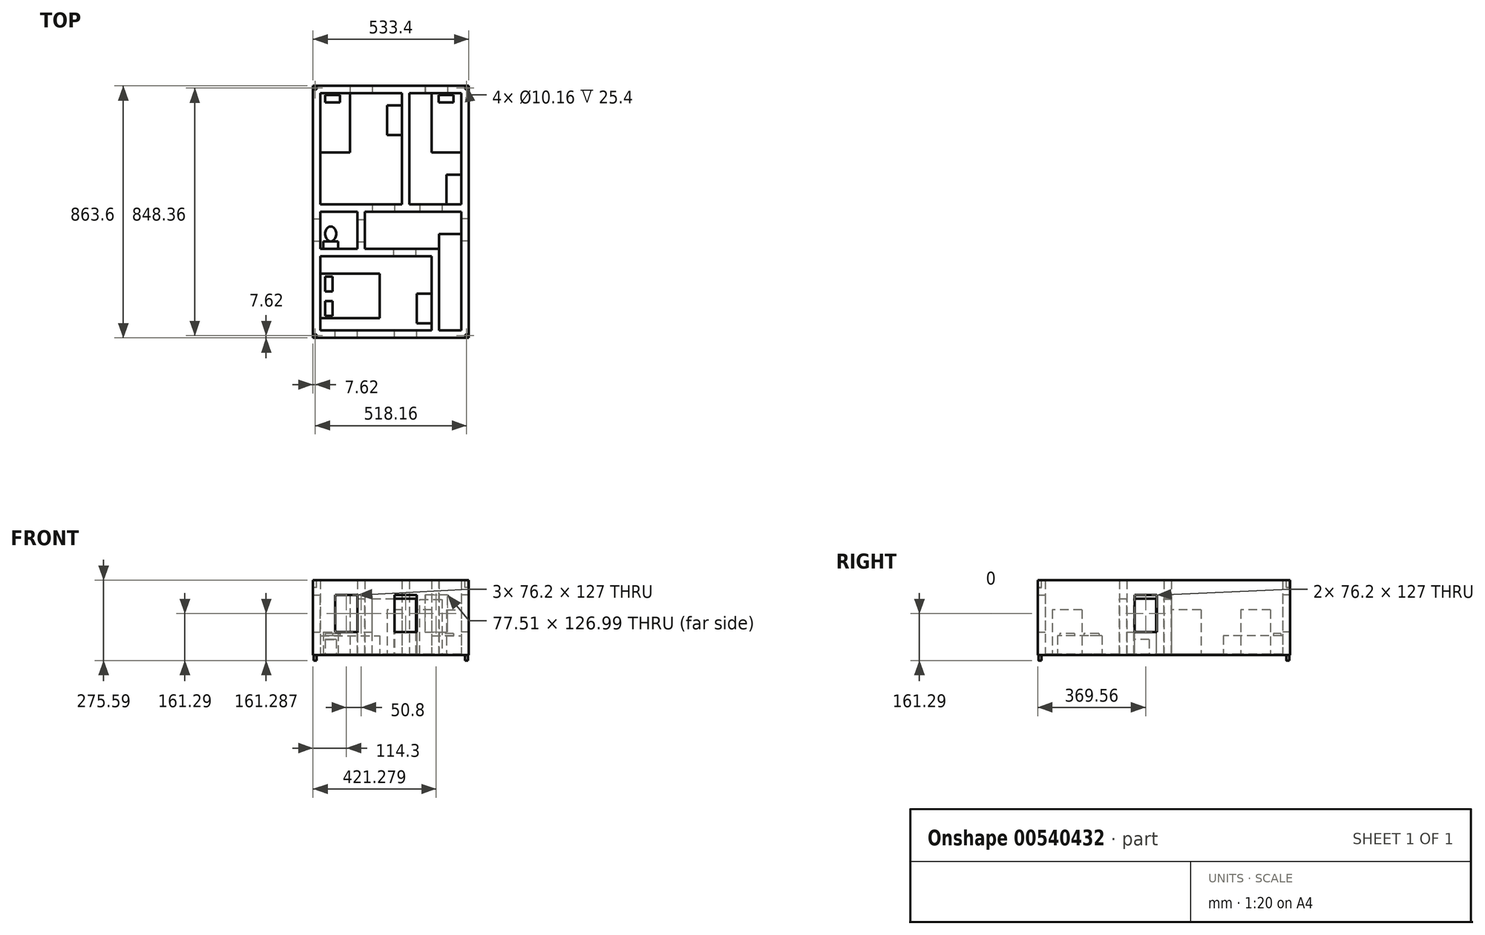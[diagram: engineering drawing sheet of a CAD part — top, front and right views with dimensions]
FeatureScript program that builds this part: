
annotation { "Feature Type Name" : "Feature", "Feature Type Description" : "" }
export const myFeature = defineFeature(function(context is Context, id is Id, definition is map)
    precondition{}
    {
        {
            var Q0;
            Q0=qCreatedBy(makeId("Top.planeOp"),FACE);
            var sketch = newSketch(context, id + "F0", { "sketchPlane" : qUnion([Q0])});
            skLineSegment(sketch, "E0.bottom", {"start": v(0, 0) * mm, "end": v(533.4, 0) * mm});
            skLineSegment(sketch, "E0.top", {"start": v(0, 863.6) * mm, "end": v(533.4, 863.6) * mm});
            skLineSegment(sketch, "E0.left", {"start": v(0, 0) * mm, "end": v(0, 863.6) * mm});
            skLineSegment(sketch, "E0.right", {"start": v(533.4, 0) * mm, "end": v(533.4, 863.6) * mm});
            skSolve(sketch);
        }
        {
            var Q0;
            Q0=makeQuery(id+"F0.imprint","IMPRINT",FACE,{"disambiguationData":[TD([[makeQuery(id+"F0.imprint","IMPRINT",EDGE,{"derivedFrom":sQuery(id+"F0.wireOp",EDGE,"E0.bottom")}),1.0]])]});
            extrude(context, id + "F1", {"entities" : qUnion([Q0]), "depth" : 2.54 * mm, "offsetDistance" : 25.4 * mm});
        }
        {
            var Q0;
            Q0=makeQuery(id+"F1.opExtrude","CAP_FACE",FACE,{"disambiguationData":[OSD([sQuery(id+"F0.wireOp",EDGE,"E0.bottom"),sQuery(id+"F0.wireOp",EDGE,"E0.top"),sQuery(id+"F0.wireOp",EDGE,"E0.left"),sQuery(id+"F0.wireOp",EDGE,"E0.right")])],"isStart":false});
            var sketch = newSketch(context, id + "F2", { "sketchPlane" : qUnion([Q0])});
            skLineSegment(sketch, "E1", {"start": v(25.4, 838.2) * mm, "end": v(25.4, 25.4) * mm});
            skLineSegment(sketch, "E2", {"start": v(25.4, 838.2) * mm, "end": v(508, 838.2) * mm});
            skLineSegment(sketch, "E3", {"start": v(508, 838.2) * mm, "end": v(508, 25.4) * mm});
            skLineSegment(sketch, "E4", {"start": v(508, 25.4) * mm, "end": v(25.4, 25.4) * mm});
            skSolve(sketch);
        }
        {
            var Q0;
            Q0=makeQuery(id+"F2.imprint","IMPRINT",FACE,{"disambiguationData":[TD([[makeQuery(id+"F2.imprint","IMPRINT",EDGE,{"derivedFrom":sQuery(id+"F2.wireOp",EDGE,"E1")}),-1.0]])]});
            extrude(context, id + "F3", {"entities" : qUnion([Q0]), "operationType" : NewBodyOperationType.ADD, "depth" : 254 * mm, "offsetDistance" : 25.4 * mm});
        }
        {
            var Q0;
            Q0=makeQuery(id+"F1.opExtrude","CAP_FACE",FACE,{"disambiguationData":[OSD([sQuery(id+"F0.wireOp",EDGE,"E0.bottom"),sQuery(id+"F0.wireOp",EDGE,"E0.top"),sQuery(id+"F0.wireOp",EDGE,"E0.left"),sQuery(id+"F0.wireOp",EDGE,"E0.right")])],"isStart":false});
            var sketch = newSketch(context, id + "F4", { "sketchPlane" : qUnion([Q0])});
            skLineSegment(sketch, "E5", {"start": v(508, 355.6) * mm, "end": v(431.8, 355.6) * mm});
            skLineSegment(sketch, "E6", {"start": v(431.8, 355.6) * mm, "end": v(431.8, 431.8) * mm});
            skLineSegment(sketch, "E7", {"start": v(431.8, 431.8) * mm, "end": v(508, 431.8) * mm});
            skLineSegment(sketch, "E8", {"start": v(508, 431.8) * mm, "end": v(508, 355.6) * mm});
            skLineSegment(sketch, "E9", {"start": v(431.8, 355.6) * mm, "end": v(228.6, 355.6) * mm});
            skLineSegment(sketch, "E10", {"start": v(508, 355.6) * mm, "end": v(508, 25.4) * mm});
            skLineSegment(sketch, "E11", {"start": v(508, 25.4) * mm, "end": v(431.8, 25.4) * mm});
            skLineSegment(sketch, "E12", {"start": v(431.8, 25.4) * mm, "end": v(431.8, 355.6) * mm});
            skSolve(sketch);
        }
        {
            var Q0;
            Q0=makeQuery(id+"F4.imprint","IMPRINT",FACE,{"disambiguationData":[TD([[makeQuery(id+"F4.imprint","IMPRINT",EDGE,{"derivedFrom":sQuery(id+"F4.wireOp",EDGE,"E5")}),1.0]])]});
            extrude(context, id + "F5", {"entities" : qUnion([Q0]), "operationType" : NewBodyOperationType.REMOVE, "oppositeDirection" : true, "depth" : 25.4 * mm, "offsetDistance" : 25.4 * mm});
        }
        {
            var Q0;
            Q0=makeQuery(id+"F1.opExtrude","CAP_FACE",FACE,{"disambiguationData":[OSD([sQuery(id+"F0.wireOp",EDGE,"E0.bottom"),sQuery(id+"F0.wireOp",EDGE,"E0.top"),sQuery(id+"F0.wireOp",EDGE,"E0.left"),sQuery(id+"F0.wireOp",EDGE,"E0.right")])],"isStart":false});
            var sketch = newSketch(context, id + "F6", { "sketchPlane" : qUnion([Q0])});
            skLineSegment(sketch, "E13", {"start": v(508, 431.8) * mm, "end": v(330.2, 431.8) * mm});
            skPoint(sketch, "E13.endSnap0", {"position": v(330.2, 838.2) * mm});
            skLineSegment(sketch, "E14", {"start": v(330.2, 431.8) * mm, "end": v(330.2, 838.2) * mm});
            skLineSegment(sketch, "E15", {"start": v(304.8, 838.2) * mm, "end": v(304.8, 431.8) * mm});
            skLineSegment(sketch, "E16", {"start": v(304.8, 431.8) * mm, "end": v(330.2, 431.8) * mm});
            skLineSegment(sketch, "E17", {"start": v(330.2, 457.2) * mm, "end": v(508, 457.2) * mm});
            skLineSegment(sketch, "E18", {"start": v(304.8, 431.8) * mm, "end": v(25.4, 431.8) * mm});
            skLineSegment(sketch, "E19", {"start": v(304.8, 457.2) * mm, "end": v(25.4, 457.2) * mm});
            skSolve(sketch);
        }
        {
            var Q0;
            Q0 = qSketchRegion(id + "F6", true);
            var Q1;
            {var subQ0=sQuery(id+"F6.wireOp",EDGE,"E13");Q1=makeQuery(id+"F6.imprint","IMPRINT",FACE,{"disambiguationData":[TD([[makeQuery(id+"F6.imprint","IMPRINT",EDGE,{"derivedFrom":subQ0}),-1.0]])]});}
            var Q2;
            {var subQ0=sQuery(id+"F6.wireOp",EDGE,"E16");Q2=makeQuery(id+"F6.imprint","IMPRINT",FACE,{"disambiguationData":[TD([[makeQuery(id+"F6.imprint","IMPRINT",EDGE,{"derivedFrom":subQ0}),1.0]])]});}
            var Q3;
            {var subQ0=sQuery(id+"F6.wireOp",EDGE,"E18");Q3=makeQuery(id+"F6.imprint","IMPRINT",FACE,{"disambiguationData":[TD([[makeQuery(id+"F6.imprint","IMPRINT",EDGE,{"derivedFrom":subQ0}),-1.0]])]});}
            extrude(context, id + "F7", {"entities" : qUnion([Q0, Q1, Q2, Q3]), "operationType" : NewBodyOperationType.ADD, "depth" : 254 * mm, "offsetDistance" : 25.4 * mm});
        }
        {
            var Q0;
            Q0=makeQuery(id+"F7.boolean.opBoolean","SPLIT",FACE,{"disambiguationData":[TD([makeQuery(id+"F3.opExtrude","SWEPT_FACE",FACE,{"disambiguationData":[OSD([sQuery(id+"F2.wireOp",EDGE,"E4")])]})])],"derivedFrom":makeQuery(id+"F1.opExtrude","CAP_FACE",FACE,{"disambiguationData":[OSD([sQuery(id+"F0.wireOp",EDGE,"E0.bottom"),sQuery(id+"F0.wireOp",EDGE,"E0.top"),sQuery(id+"F0.wireOp",EDGE,"E0.left"),sQuery(id+"F0.wireOp",EDGE,"E0.right")])],"isStart":false})});
            var sketch = newSketch(context, id + "F8", { "sketchPlane" : qUnion([Q0])});
            skLineSegment(sketch, "E20", {"start": v(25.4, 304.8) * mm, "end": v(431.8, 304.8) * mm});
            skLineSegment(sketch, "E21", {"start": v(152.4, 431.8) * mm, "end": v(152.4, 304.8) * mm});
            skLineSegment(sketch, "E22", {"start": v(431.8, 279.4) * mm, "end": v(25.4, 279.4) * mm});
            skLineSegment(sketch, "E23", {"start": v(406.4, 279.4) * mm, "end": v(406.4, 25.4) * mm});
            skLineSegment(sketch, "E24", {"start": v(177.8, 431.8) * mm, "end": v(177.8, 304.8) * mm});
            skSolve(sketch);
        }
        {
            var Q0;
            Q0 = qSketchRegion(id + "F8", true);
            var Q1;
            {var subQ4=sQuery(id+"F8.wireOp",EDGE,"E20");var subQ7=makeQuery(id+"F8.imprint","INTERSECT",VERTEX,{"derivedFrom":[subQ4,sQuery(id+"F8.wireOp",EDGE,"E21")]});Q1=makeQuery(id+"F8.imprint","IMPRINT",FACE,{"disambiguationData":[TD([[makeQuery(id+"F8.imprint","IMPRINT",EDGE,{"disambiguationData":[TD([[subQ7,-1.0]])],"derivedFrom":subQ4}),-1.0]])]});}
            var Q2;
            {var subQ3=sQuery(id+"F8.wireOp",EDGE,"E23");Q2=makeQuery(id+"F8.imprint","IMPRINT",FACE,{"disambiguationData":[TD([[makeQuery(id+"F8.imprint","IMPRINT",EDGE,{"derivedFrom":subQ3}),1.0]])]});}
            var Q3;
            {var subQ0=sQuery(id+"F8.wireOp",EDGE,"E21");Q3=makeQuery(id+"F8.imprint","IMPRINT",FACE,{"disambiguationData":[TD([[makeQuery(id+"F8.imprint","IMPRINT",EDGE,{"derivedFrom":subQ0}),1.0]])]});}
            extrude(context, id + "F9", {"entities" : qUnion([Q0, Q1, Q2, Q3]), "operationType" : NewBodyOperationType.ADD, "depth" : 254 * mm, "offsetDistance" : 25.4 * mm});
        }
        {
            var Q0;
            {var subQ1=sQuery(id+"F2.wireOp",EDGE,"E3");var subQ8=sQuery(id+"F6.wireOp",EDGE,"E18");var subQ9=sQuery(id+"F6.wireOp",EDGE,"E16");var subQ10=sQuery(id+"F6.wireOp",EDGE,"E13");Q0=makeQuery(id+"F9.boolean.opBoolean","SPLIT",FACE,{"disambiguationData":[TD([makeQuery(id+"F3.opExtrude","SWEPT_FACE",FACE,{"disambiguationData":[OSD([subQ1])]})])],"derivedFrom":makeQuery(id+"F7.opExtrude","SWEPT_FACE",FACE,{"disambiguationData":[OSD([subQ10,subQ9,subQ8])]})});}
            var sketch = newSketch(context, id + "F10", { "sketchPlane" : qUnion([Q0])});
            skLineSegment(sketch, "E25", {"start": v(202.22, 2.54) * mm, "end": v(202.22, 193.04) * mm});
            skLineSegment(sketch, "E26", {"start": v(202.22, 193.04) * mm, "end": v(278.42, 193.04) * mm});
            skLineSegment(sketch, "E27", {"start": v(278.42, 193.04) * mm, "end": v(278.42, 2.54) * mm});
            skLineSegment(sketch, "E28", {"start": v(278.42, 2.54) * mm, "end": v(202.22, 2.54) * mm});
            skLineSegment(sketch, "E29", {"start": v(364.65, 2.54) * mm, "end": v(364.65, 190.5) * mm});
            skLineSegment(sketch, "E30", {"start": v(364.65, 190.5) * mm, "end": v(440.85, 190.5) * mm});
            skLineSegment(sketch, "E31", {"start": v(440.85, 190.5) * mm, "end": v(440.85, 0) * mm});
            skLineSegment(sketch, "E32", {"start": v(440.85, 0) * mm, "end": v(364.65, 2.54) * mm});
            skSolve(sketch);
        }
        {
            var Q0;
            Q0=makeQuery(id+"F10.imprint","IMPRINT",FACE,{"disambiguationData":[TD([[makeQuery(id+"F10.imprint","IMPRINT",EDGE,{"derivedFrom":sQuery(id+"F10.wireOp",EDGE,"E25")}),-1.0]])]});
            var Q1;
            {var subQ0=sQuery(id+"F10.wireOp",EDGE,"E29");Q1=makeQuery(id+"F10.imprint","IMPRINT",FACE,{"disambiguationData":[TD([[makeQuery(id+"F10.imprint","IMPRINT",EDGE,{"derivedFrom":subQ0}),-1.0]])]});}
            extrude(context, id + "F11", {"entities" : qUnion([Q0, Q1]), "operationType" : NewBodyOperationType.REMOVE, "oppositeDirection" : true, "depth" : 25.4 * mm, "offsetDistance" : 25.4 * mm});
        }
        {
            var Q0;
            Q0=makeQuery(id+"F9.opExtrude","SWEPT_FACE",FACE,{"disambiguationData":[OSD([sQuery(id+"F8.wireOp",EDGE,"E24")])]});
            var sketch = newSketch(context, id + "F12", { "sketchPlane" : qUnion([Q0])});
            skLineSegment(sketch, "E33", {"start": v(329.52, 2.54) * mm, "end": v(329.52, 193.04) * mm});
            skLineSegment(sketch, "E34", {"start": v(329.52, 193.04) * mm, "end": v(405.72, 193.04) * mm});
            skLineSegment(sketch, "E35", {"start": v(405.72, 193.04) * mm, "end": v(405.72, 2.54) * mm});
            skLineSegment(sketch, "E36", {"start": v(405.72, 2.54) * mm, "end": v(329.52, 2.54) * mm});
            skSolve(sketch);
        }
        {
            var Q0;
            Q0 = qSketchRegion(id + "F12", true);
            extrude(context, id + "F13", {"entities" : qUnion([Q0]), "operationType" : NewBodyOperationType.REMOVE, "oppositeDirection" : true, "depth" : 25.4 * mm, "offsetDistance" : 25.4 * mm});
        }
        {
            var Q0;
            {var subQ0=sQuery(id+"F8.wireOp",EDGE,"E20");Q0=makeQuery(id+"F9.opExtrude","SWEPT_FACE",FACE,{"disambiguationData":[OSD([subQ0]),TDD([makeQuery(id+"F8.imprint","IMPRINT",EDGE,{"disambiguationData":[TD([[makeQuery(id+"F8.imprint","INTERSECT",VERTEX,{"derivedFrom":[makeQuery(id+"F5.boolean.opBoolean","COPY",EDGE,{"derivedFrom":makeQuery(id+"F5.opExtrude","CAP_EDGE",EDGE,{"disambiguationData":[OSD([sQuery(id+"F4.wireOp",EDGE,"E12")])],"isStart":true})}),subQ0]}),1.0]])],"derivedFrom":subQ0})])]});}
            var sketch = newSketch(context, id + "F14", { "sketchPlane" : qUnion([Q0])});
            skLineSegment(sketch, "E37", {"start": v(-352.2, 2.54) * mm, "end": v(-352.2, 193.04) * mm});
            skLineSegment(sketch, "E38", {"start": v(-352.2, 193.04) * mm, "end": v(-276, 193.04) * mm});
            skLineSegment(sketch, "E39", {"start": v(-276, 193.04) * mm, "end": v(-276, 0) * mm});
            skLineSegment(sketch, "E40", {"start": v(-276, 0) * mm, "end": v(-352.2, 2.54) * mm});
            skSolve(sketch);
        }
        {
            var Q0;
            {var subQ0=sQuery(id+"F14.wireOp",EDGE,"E37");Q0=makeQuery(id+"F14.imprint","IMPRINT",FACE,{"disambiguationData":[TD([[makeQuery(id+"F14.imprint","IMPRINT",EDGE,{"derivedFrom":subQ0}),-1.0]])]});}
            extrude(context, id + "F15", {"entities" : qUnion([Q0]), "operationType" : NewBodyOperationType.REMOVE, "oppositeDirection" : true, "depth" : 25.4 * mm, "offsetDistance" : 25.4 * mm});
        }
        {
            var Q0;
            {var subQ0=sQuery(id+"F2.wireOp",EDGE,"E3");var subQ1=sQuery(id+"F2.wireOp",EDGE,"E2");Q0=makeQuery(id+"F7.boolean.opBoolean","SPLIT",FACE,{"disambiguationData":[TD([makeQuery(id+"F3.opExtrude","SWEPT_FACE",FACE,{"disambiguationData":[OSD([subQ0])]})])],"derivedFrom":makeQuery(id+"F3.opExtrude","SWEPT_FACE",FACE,{"disambiguationData":[OSD([subQ1])]})});}
            var sketch = newSketch(context, id + "F16", { "sketchPlane" : qUnion([Q0])});
            skLineSegment(sketch, "E41", {"start": v(382.52, 78.74) * mm, "end": v(460.04, 78.74) * mm});
            skLineSegment(sketch, "E42", {"start": v(460.04, 78.74) * mm, "end": v(460.04, 205.73) * mm});
            skLineSegment(sketch, "E43", {"start": v(460.04, 205.73) * mm, "end": v(383.84, 205.73) * mm});
            skLineSegment(sketch, "E44", {"start": v(383.84, 205.73) * mm, "end": v(382.52, 78.74) * mm});
            skLineSegment(sketch, "E45.0", {"start": v(330.2, 2.54) * mm, "end": v(508, 2.54) * mm});
            skLineSegment(sketch, "E46.0", {"start": v(330.2, 256.54) * mm, "end": v(330.2, 2.54) * mm});
            skSolve(sketch);
        }
        {
            var Q0;
            Q0 = qSketchRegion(id + "F16", true);
            extrude(context, id + "F17", {"entities" : qUnion([Q0]), "operationType" : NewBodyOperationType.REMOVE, "oppositeDirection" : true, "depth" : 25.4 * mm, "offsetDistance" : 25.4 * mm});
        }
        {
            var Q0;
            {var subQ1=sQuery(id+"F2.wireOp",EDGE,"E2");var subQ2=sQuery(id+"F2.wireOp",EDGE,"E1");Q0=makeQuery(id+"F7.boolean.opBoolean","SPLIT",FACE,{"disambiguationData":[TD([makeQuery(id+"F3.opExtrude","SWEPT_FACE",FACE,{"disambiguationData":[OSD([subQ2])]})])],"derivedFrom":makeQuery(id+"F3.opExtrude","SWEPT_FACE",FACE,{"disambiguationData":[OSD([subQ1])]})});}
            var sketch = newSketch(context, id + "F18", { "sketchPlane" : qUnion([Q0])});
            skLineSegment(sketch, "E47", {"start": v(127, 78.74) * mm, "end": v(203.2, 78.74) * mm});
            skLineSegment(sketch, "E48", {"start": v(203.2, 78.74) * mm, "end": v(203.2, 205.74) * mm});
            skLineSegment(sketch, "E49", {"start": v(203.2, 205.74) * mm, "end": v(127, 205.74) * mm});
            skLineSegment(sketch, "E50", {"start": v(127, 205.74) * mm, "end": v(127, 78.74) * mm});
            skLineSegment(sketch, "E51.0", {"start": v(304.8, 256.54) * mm, "end": v(304.8, 2.54) * mm});
            skLineSegment(sketch, "E52.0", {"start": v(25.4, 2.54) * mm, "end": v(304.8, 2.54) * mm});
            skSolve(sketch);
        }
        {
            var Q0;
            Q0 = qSketchRegion(id + "F18", true);
            extrude(context, id + "F19", {"entities" : qUnion([Q0]), "operationType" : NewBodyOperationType.REMOVE, "oppositeDirection" : true, "depth" : 25.4 * mm, "offsetDistance" : 25.4 * mm});
        }
        {
            var Q0;
            {var subQ0=sQuery(id+"F6.wireOp",EDGE,"E18");var subQ1=sQuery(id+"F6.wireOp",EDGE,"E16");var subQ2=sQuery(id+"F6.wireOp",EDGE,"E13");var subQ3=makeQuery(id+"F7.opExtrude","SWEPT_FACE",FACE,{"disambiguationData":[OSD([subQ2,subQ1,subQ0])]});var subQ9=sQuery(id+"F2.wireOp",EDGE,"E4");var subQ12=sQuery(id+"F2.wireOp",EDGE,"E1");var subQ17=makeQuery(id+"F3.opExtrude","SWEPT_FACE",FACE,{"disambiguationData":[OSD([subQ9])]});var subQ18=makeQuery(id+"F3.opExtrude","SWEPT_FACE",FACE,{"disambiguationData":[OSD([subQ12])]});Q0=makeQuery(id+"F9.boolean.opBoolean","SPLIT",FACE,{"disambiguationData":[TD([subQ3])],"derivedFrom":makeQuery(id+"F7.boolean.opBoolean","SPLIT",FACE,{"disambiguationData":[TD([subQ17])],"derivedFrom":subQ18})});}
            var sketch = newSketch(context, id + "F20", { "sketchPlane" : qUnion([Q0])});
            skLineSegment(sketch, "E53", {"start": v(331.46, 205.74) * mm, "end": v(331.46, 78.74) * mm});
            skLineSegment(sketch, "E54", {"start": v(331.46, 78.74) * mm, "end": v(407.66, 78.74) * mm});
            skLineSegment(sketch, "E55", {"start": v(407.66, 78.74) * mm, "end": v(407.66, 205.74) * mm});
            skLineSegment(sketch, "E56", {"start": v(407.66, 205.74) * mm, "end": v(331.46, 205.74) * mm});
            skLineSegment(sketch, "E57.0", {"start": v(431.8, 2.54) * mm, "end": v(304.8, 2.54) * mm});
            skSolve(sketch);
        }
        {
            var Q0;
            Q0 = qSketchRegion(id + "F20", true);
            extrude(context, id + "F21", {"entities" : qUnion([Q0]), "operationType" : NewBodyOperationType.REMOVE, "oppositeDirection" : true, "depth" : 25.4 * mm, "offsetDistance" : 25.4 * mm});
        }
        {
            var Q0;
            {var subQ0=sQuery(id+"F2.wireOp",EDGE,"E4");var subQ3=sQuery(id+"F2.wireOp",EDGE,"E1");Q0=makeQuery(id+"F9.boolean.opBoolean","SPLIT",FACE,{"disambiguationData":[TD([makeQuery(id+"F3.opExtrude","SWEPT_FACE",FACE,{"disambiguationData":[OSD([subQ3])]})])],"derivedFrom":makeQuery(id+"F5.boolean.opBoolean","MERGE",FACE,{"derivedFrom":[makeQuery(id+"F3.opExtrude","SWEPT_FACE",FACE,{"disambiguationData":[OSD([subQ0])]}),makeQuery(id+"F5.opExtrude","SWEPT_FACE",FACE,{"disambiguationData":[OSD([sQuery(id+"F4.wireOp",EDGE,"E11")])]})]})});}
            var sketch = newSketch(context, id + "F22", { "sketchPlane" : qUnion([Q0])});
            skLineSegment(sketch, "E58.bottom", {"start": v(-279.4, 205.74) * mm, "end": v(-355.6, 205.74) * mm});
            skLineSegment(sketch, "E58.top", {"start": v(-279.4, 78.74) * mm, "end": v(-355.6, 78.74) * mm});
            skLineSegment(sketch, "E58.left", {"start": v(-279.4, 205.74) * mm, "end": v(-279.4, 78.74) * mm});
            skLineSegment(sketch, "E58.right", {"start": v(-355.6, 205.74) * mm, "end": v(-355.6, 78.74) * mm});
            skPoint(sketch, "E58.middle", {"position": v(-317.5, 142.24) * mm});
            skLineSegment(sketch, "E59.0", {"start": v(-406.4, 256.54) * mm, "end": v(-406.4, 2.54) * mm});
            skLineSegment(sketch, "E60.bottom", {"start": v(-76.2, 205.74) * mm, "end": v(-152.4, 205.74) * mm});
            skLineSegment(sketch, "E60.top", {"start": v(-76.2, 78.74) * mm, "end": v(-152.4, 78.74) * mm});
            skLineSegment(sketch, "E60.left", {"start": v(-76.2, 205.74) * mm, "end": v(-76.2, 78.74) * mm});
            skLineSegment(sketch, "E60.right", {"start": v(-152.4, 205.74) * mm, "end": v(-152.4, 78.74) * mm});
            skPoint(sketch, "E60.middle", {"position": v(-114.3, 142.24) * mm});
            skSolve(sketch);
        }
        {
            var Q0;
            Q0 = qSketchRegion(id + "F22", true);
            extrude(context, id + "F23", {"entities" : qUnion([Q0]), "operationType" : NewBodyOperationType.REMOVE, "oppositeDirection" : true, "depth" : 25.4 * mm, "offsetDistance" : 25.4 * mm});
        }
        {
            var Q0;
            {var subQ0=sQuery(id+"F2.wireOp",EDGE,"E4");var subQ1=sQuery(id+"F2.wireOp",EDGE,"E3");Q0=makeQuery(id+"F7.boolean.opBoolean","SPLIT",FACE,{"disambiguationData":[TD([makeQuery(id+"F3.opExtrude","SWEPT_FACE",FACE,{"disambiguationData":[OSD([subQ0])]})])],"derivedFrom":makeQuery(id+"F5.boolean.opBoolean","MERGE",FACE,{"derivedFrom":[makeQuery(id+"F3.opExtrude","SWEPT_FACE",FACE,{"disambiguationData":[OSD([subQ1])]}),makeQuery(id+"F5.opExtrude","SWEPT_FACE",FACE,{"disambiguationData":[OSD([sQuery(id+"F4.wireOp",EDGE,"E10")])]})]})});}
            var sketch = newSketch(context, id + "F24", { "sketchPlane" : qUnion([Q0])});
            skLineSegment(sketch, "E61.0", {"start": v(-407.66, 205.74) * mm, "end": v(-331.46, 205.74) * mm});
            skLineSegment(sketch, "E62.0", {"start": v(-407.66, 78.74) * mm, "end": v(-407.66, 205.74) * mm});
            skLineSegment(sketch, "E63.0", {"start": v(-331.46, 78.74) * mm, "end": v(-407.66, 78.74) * mm});
            skLineSegment(sketch, "E64.0", {"start": v(-331.46, 205.74) * mm, "end": v(-331.46, 78.74) * mm});
            skSolve(sketch);
        }
        {
            var Q0;
            Q0 = qSketchRegion(id + "F24", true);
            extrude(context, id + "F25", {"entities" : qUnion([Q0]), "operationType" : NewBodyOperationType.REMOVE, "oppositeDirection" : true, "depth" : 25.4 * mm, "offsetDistance" : 25.4 * mm});
        }
        {
            var Q0;
            Q0=makeQuery(id+"F1.opExtrude","CAP_FACE",FACE,{"disambiguationData":[OSD([sQuery(id+"F0.wireOp",EDGE,"E0.bottom"),sQuery(id+"F0.wireOp",EDGE,"E0.top"),sQuery(id+"F0.wireOp",EDGE,"E0.left"),sQuery(id+"F0.wireOp",EDGE,"E0.right")])],"isStart":true});
            var sketch = newSketch(context, id + "F26", { "sketchPlane" : qUnion([Q0])});
            skCircle(sketch, "E65", {"center": v(7.62, -7.62) * mm, "radius": 5.08 * mm});
            skCircle(sketch, "E66", {"center": v(525.78, -7.62) * mm, "radius": 5.08 * mm});
            skCircle(sketch, "E67", {"center": v(525.78, -855.98) * mm, "radius": 5.08 * mm});
            skCircle(sketch, "E68", {"center": v(7.62, -855.98) * mm, "radius": 5.08 * mm});
            skSolve(sketch);
        }
        {
            var Q0;
            Q0 = qSketchRegion(id + "F26", true);
            extrude(context, id + "F27", {"entities" : qUnion([Q0]), "operationType" : NewBodyOperationType.ADD, "depth" : 19.05 * mm, "offsetDistance" : 25.4 * mm});
        }
        {
            var Q0;
            {var subQ0=sQuery(id+"F6.wireOp",EDGE,"E18");var subQ1=sQuery(id+"F6.wireOp",EDGE,"E16");var subQ2=sQuery(id+"F6.wireOp",EDGE,"E13");var subQ3=sQuery(id+"F2.wireOp",EDGE,"E4");var subQ4=sQuery(id+"F2.wireOp",EDGE,"E1");var subQ5=sQuery(id+"F2.wireOp",EDGE,"E3");var subQ6=sQuery(id+"F2.wireOp",EDGE,"E2");Q0=makeQuery(id+"F9.boolean.opBoolean","MERGE",FACE,{"derivedFrom":[makeQuery(id+"F7.boolean.opBoolean","MERGE",FACE,{"derivedFrom":[makeQuery(id+"F3.opExtrude","CAP_FACE",FACE,{"disambiguationData":[OSD([sQuery(id+"F0.wireOp",EDGE,"E0.bottom"),sQuery(id+"F0.wireOp",EDGE,"E0.top"),sQuery(id+"F0.wireOp",EDGE,"E0.left"),sQuery(id+"F0.wireOp",EDGE,"E0.right"),subQ4,subQ6,subQ5,subQ3])],"isStart":false}),makeQuery(id+"F7.opExtrude","CAP_FACE",FACE,{"disambiguationData":[OSD([subQ4,subQ6,subQ5,subQ2,sQuery(id+"F6.wireOp",EDGE,"E14"),sQuery(id+"F6.wireOp",EDGE,"E15"),subQ1,sQuery(id+"F6.wireOp",EDGE,"E17"),subQ0,sQuery(id+"F6.wireOp",EDGE,"E19")])],"isStart":false})]}),makeQuery(id+"F9.opExtrude","CAP_FACE",FACE,{"disambiguationData":[OSD([subQ4,subQ3,sQuery(id+"F4.wireOp",EDGE,"E12"),subQ2,subQ1,subQ0,sQuery(id+"F8.wireOp",EDGE,"E20"),sQuery(id+"F8.wireOp",EDGE,"E21"),sQuery(id+"F8.wireOp",EDGE,"E22"),sQuery(id+"F8.wireOp",EDGE,"E23"),sQuery(id+"F8.wireOp",EDGE,"E24")])],"isStart":false})]});}
            var sketch = newSketch(context, id + "F28", { "sketchPlane" : qUnion([Q0])});
            skCircle(sketch, "E69", {"center": v(7.62, 7.62) * mm, "radius": 5.08 * mm});
            skCircle(sketch, "E70", {"center": v(525.78, 7.62) * mm, "radius": 5.08 * mm});
            skCircle(sketch, "E71", {"center": v(525.78, 855.98) * mm, "radius": 5.08 * mm});
            skCircle(sketch, "E72", {"center": v(7.62, 855.98) * mm, "radius": 5.08 * mm});
            skSolve(sketch);
        }
        {
            var Q0;
            Q0 = qSketchRegion(id + "F28", true);
            extrude(context, id + "F29", {"entities" : qUnion([Q0]), "operationType" : NewBodyOperationType.REMOVE, "oppositeDirection" : true, "depth" : 25.4 * mm, "offsetDistance" : 25.4 * mm});
        }
        {
            var Q0;
            {var subQ0=sQuery(id+"F8.wireOp",EDGE,"E20");var subQ1=sQuery(id+"F6.wireOp",EDGE,"E18");var subQ2=sQuery(id+"F6.wireOp",EDGE,"E16");var subQ3=sQuery(id+"F6.wireOp",EDGE,"E13");var subQ10=makeQuery(id+"F3.opExtrude","SWEPT_FACE",FACE,{"disambiguationData":[OSD([sQuery(id+"F2.wireOp",EDGE,"E3")])]});var subQ11=makeQuery(id+"F3.opExtrude","SWEPT_FACE",FACE,{"disambiguationData":[OSD([sQuery(id+"F2.wireOp",EDGE,"E4")])]});var subQ15=makeQuery(id+"F1.opExtrude","CAP_FACE",FACE,{"disambiguationData":[OSD([sQuery(id+"F0.wireOp",EDGE,"E0.bottom"),sQuery(id+"F0.wireOp",EDGE,"E0.top"),sQuery(id+"F0.wireOp",EDGE,"E0.left"),sQuery(id+"F0.wireOp",EDGE,"E0.right")])],"isStart":false});var subQ16=subQ15;var subQ17=makeQuery(id+"F7.boolean.opBoolean","SPLIT",FACE,{"disambiguationData":[TD([subQ11])],"derivedFrom":subQ16});var subQ19=sQuery(id+"F8.wireOp",EDGE,"E21");Q0=makeQuery(id+"F15.boolean.opBoolean","MERGE",FACE,{"derivedFrom":[makeQuery(id+"F9.boolean.opBoolean","SPLIT",FACE,{"disambiguationData":[TD([subQ11])],"derivedFrom":subQ17}),makeQuery(id+"F13.boolean.opBoolean","MERGE",FACE,{"derivedFrom":[makeQuery(id+"F9.boolean.opBoolean","SPLIT",FACE,{"disambiguationData":[TD([makeQuery(id+"F9.opExtrude","SWEPT_FACE",FACE,{"disambiguationData":[OSD([subQ19])]})])],"derivedFrom":subQ17}),makeQuery(id+"F11.boolean.opBoolean","MERGE",FACE,{"derivedFrom":[makeQuery(id+"F7.boolean.opBoolean","SPLIT",FACE,{"disambiguationData":[TD([makeQuery(id+"F7.opExtrude","SWEPT_FACE",FACE,{"disambiguationData":[OSD([sQuery(id+"F6.wireOp",EDGE,"E14")])]})])],"derivedFrom":subQ16}),makeQuery(id+"F7.boolean.opBoolean","SPLIT",FACE,{"disambiguationData":[TD([makeQuery(id+"F7.opExtrude","SWEPT_FACE",FACE,{"disambiguationData":[OSD([sQuery(id+"F6.wireOp",EDGE,"E15")])]})])],"derivedFrom":subQ16}),makeQuery(id+"F9.boolean.opBoolean","SPLIT",FACE,{"disambiguationData":[TD([subQ10])],"derivedFrom":subQ17}),makeQuery(id+"F11.opExtrude","SWEPT_FACE",FACE,{"disambiguationData":[OSD([sQuery(id+"F10.wireOp",EDGE,"E28")])]}),makeQuery(id+"F11.opExtrude","SWEPT_FACE",FACE,{"disambiguationData":[OSD([subQ3,subQ2,subQ1])]})]}),makeQuery(id+"F13.opExtrude","SWEPT_FACE",FACE,{"disambiguationData":[OSD([sQuery(id+"F12.wireOp",EDGE,"E36")])]})]}),makeQuery(id+"F15.opExtrude","SWEPT_FACE",FACE,{"disambiguationData":[OSD([subQ0])]})]});}
            var sketch = newSketch(context, id + "F30", { "sketchPlane" : qUnion([Q0])});
            skLineSegment(sketch, "E73", {"start": v(127, 838.2) * mm, "end": v(127, 635) * mm});
            skLineSegment(sketch, "E74", {"start": v(127, 635) * mm, "end": v(25.4, 635) * mm});
            skLineSegment(sketch, "E75", {"start": v(25.4, 635) * mm, "end": v(25.4, 838.2) * mm});
            skLineSegment(sketch, "E76", {"start": v(25.4, 838.2) * mm, "end": v(127, 838.2) * mm});
            skLineSegment(sketch, "E77", {"start": v(508, 635) * mm, "end": v(406.4, 635) * mm});
            skLineSegment(sketch, "E78", {"start": v(406.4, 635) * mm, "end": v(406.4, 838.2) * mm});
            skLineSegment(sketch, "E79", {"start": v(406.4, 838.2) * mm, "end": v(508, 838.2) * mm});
            skLineSegment(sketch, "E80", {"start": v(508, 838.2) * mm, "end": v(508, 635) * mm});
            skLineSegment(sketch, "E81", {"start": v(25.4, 68.1) * mm, "end": v(25.4, 220.5) * mm});
            skLineSegment(sketch, "E82", {"start": v(25.4, 220.5) * mm, "end": v(228.6, 220.5) * mm});
            skLineSegment(sketch, "E83", {"start": v(228.6, 220.5) * mm, "end": v(228.6, 68.1) * mm});
            skLineSegment(sketch, "E84", {"start": v(228.6, 68.1) * mm, "end": v(25.4, 68.1) * mm});
            skSolve(sketch);
        }
        {
            var Q0;
            Q0 = qSketchRegion(id + "F30", true);
            extrude(context, id + "F31", {"entities" : qUnion([Q0]), "operationType" : NewBodyOperationType.ADD, "depth" : 63.5 * mm, "offsetDistance" : 25.4 * mm});
        }
        {
            var Q0;
            Q0=makeQuery(id+"F31.opExtrude","CAP_FACE",FACE,{"disambiguationData":[OSD([sQuery(id+"F30.wireOp",EDGE,"E81"),sQuery(id+"F30.wireOp",EDGE,"E82"),sQuery(id+"F30.wireOp",EDGE,"E83"),sQuery(id+"F30.wireOp",EDGE,"E84")])],"isStart":false});
            var sketch = newSketch(context, id + "F32", { "sketchPlane" : qUnion([Q0])});
            skLineSegment(sketch, "E85.bottom", {"start": v(91.83, 831.83) * mm, "end": v(41.03, 831.83) * mm});
            skLineSegment(sketch, "E85.top", {"start": v(91.83, 806.43) * mm, "end": v(41.03, 806.43) * mm});
            skLineSegment(sketch, "E85.left", {"start": v(91.83, 831.83) * mm, "end": v(91.83, 806.43) * mm});
            skLineSegment(sketch, "E85.right", {"start": v(41.03, 831.83) * mm, "end": v(41.03, 806.43) * mm});
            skPoint(sketch, "E85.middle", {"position": v(66.43, 819.13) * mm});
            skLineSegment(sketch, "E86.bottom", {"start": v(481.35, 806.43) * mm, "end": v(430.55, 806.43) * mm});
            skLineSegment(sketch, "E86.top", {"start": v(481.35, 831.83) * mm, "end": v(430.55, 831.83) * mm});
            skLineSegment(sketch, "E86.left", {"start": v(481.35, 806.43) * mm, "end": v(481.35, 831.83) * mm});
            skLineSegment(sketch, "E86.right", {"start": v(430.55, 806.43) * mm, "end": v(430.55, 831.83) * mm});
            skPoint(sketch, "E86.middle", {"position": v(455.95, 819.13) * mm});
            skLineSegment(sketch, "E87.bottom", {"start": v(66.43, 126.48) * mm, "end": v(41.03, 126.48) * mm});
            skLineSegment(sketch, "E87.top", {"start": v(66.43, 75.68) * mm, "end": v(41.03, 75.68) * mm});
            skLineSegment(sketch, "E87.left", {"start": v(66.43, 126.48) * mm, "end": v(66.43, 75.68) * mm});
            skLineSegment(sketch, "E87.right", {"start": v(41.03, 126.48) * mm, "end": v(41.03, 75.68) * mm});
            skPoint(sketch, "E87.middle", {"position": v(53.73, 101.08) * mm});
            skLineSegment(sketch, "E88.bottom", {"start": v(66.43, 209.41) * mm, "end": v(41.03, 209.41) * mm});
            skLineSegment(sketch, "E88.top", {"start": v(66.43, 158.61) * mm, "end": v(41.03, 158.61) * mm});
            skLineSegment(sketch, "E88.left", {"start": v(66.43, 209.41) * mm, "end": v(66.43, 158.61) * mm});
            skLineSegment(sketch, "E88.right", {"start": v(41.03, 209.41) * mm, "end": v(41.03, 158.61) * mm});
            skPoint(sketch, "E88.middle", {"position": v(53.73, 184.01) * mm});
            skPoint(sketch, "E88.middle.positionSnap0", {"position": v(53.73, 126.48) * mm});
            skPoint(sketch, "E88.centerSnap0", {"position": v(53.73, 126.48) * mm});
            skSolve(sketch);
        }
        {
            var Q0;
            Q0 = qSketchRegion(id + "F32", true);
            extrude(context, id + "F33", {"entities" : qUnion([Q0]), "operationType" : NewBodyOperationType.ADD, "depth" : 7.62 * mm, "offsetDistance" : 25.4 * mm});
        }
        {
            var Q0;
            {var subQ0=sQuery(id+"F8.wireOp",EDGE,"E20");var subQ1=sQuery(id+"F6.wireOp",EDGE,"E18");var subQ2=sQuery(id+"F6.wireOp",EDGE,"E16");var subQ3=sQuery(id+"F6.wireOp",EDGE,"E13");var subQ10=makeQuery(id+"F3.opExtrude","SWEPT_FACE",FACE,{"disambiguationData":[OSD([sQuery(id+"F2.wireOp",EDGE,"E3")])]});var subQ11=makeQuery(id+"F3.opExtrude","SWEPT_FACE",FACE,{"disambiguationData":[OSD([sQuery(id+"F2.wireOp",EDGE,"E4")])]});var subQ15=makeQuery(id+"F1.opExtrude","CAP_FACE",FACE,{"disambiguationData":[OSD([sQuery(id+"F0.wireOp",EDGE,"E0.bottom"),sQuery(id+"F0.wireOp",EDGE,"E0.top"),sQuery(id+"F0.wireOp",EDGE,"E0.left"),sQuery(id+"F0.wireOp",EDGE,"E0.right")])],"isStart":false});var subQ16=subQ15;var subQ17=makeQuery(id+"F7.boolean.opBoolean","SPLIT",FACE,{"disambiguationData":[TD([subQ11])],"derivedFrom":subQ16});var subQ19=sQuery(id+"F8.wireOp",EDGE,"E21");Q0=makeQuery(id+"F15.boolean.opBoolean","MERGE",FACE,{"derivedFrom":[makeQuery(id+"F9.boolean.opBoolean","SPLIT",FACE,{"disambiguationData":[TD([subQ11])],"derivedFrom":subQ17}),makeQuery(id+"F13.boolean.opBoolean","MERGE",FACE,{"derivedFrom":[makeQuery(id+"F9.boolean.opBoolean","SPLIT",FACE,{"disambiguationData":[TD([makeQuery(id+"F9.opExtrude","SWEPT_FACE",FACE,{"disambiguationData":[OSD([subQ19])]})])],"derivedFrom":subQ17}),makeQuery(id+"F11.boolean.opBoolean","MERGE",FACE,{"derivedFrom":[makeQuery(id+"F7.boolean.opBoolean","SPLIT",FACE,{"disambiguationData":[TD([makeQuery(id+"F7.opExtrude","SWEPT_FACE",FACE,{"disambiguationData":[OSD([sQuery(id+"F6.wireOp",EDGE,"E14")])]})])],"derivedFrom":subQ16}),makeQuery(id+"F7.boolean.opBoolean","SPLIT",FACE,{"disambiguationData":[TD([makeQuery(id+"F7.opExtrude","SWEPT_FACE",FACE,{"disambiguationData":[OSD([sQuery(id+"F6.wireOp",EDGE,"E15")])]})])],"derivedFrom":subQ16}),makeQuery(id+"F9.boolean.opBoolean","SPLIT",FACE,{"disambiguationData":[TD([subQ10])],"derivedFrom":subQ17}),makeQuery(id+"F11.opExtrude","SWEPT_FACE",FACE,{"disambiguationData":[OSD([sQuery(id+"F10.wireOp",EDGE,"E28")])]}),makeQuery(id+"F11.opExtrude","SWEPT_FACE",FACE,{"disambiguationData":[OSD([subQ3,subQ2,subQ1])]})]}),makeQuery(id+"F13.opExtrude","SWEPT_FACE",FACE,{"disambiguationData":[OSD([sQuery(id+"F12.wireOp",EDGE,"E36")])]})]}),makeQuery(id+"F15.opExtrude","SWEPT_FACE",FACE,{"disambiguationData":[OSD([subQ0])]})]});}
            var sketch = newSketch(context, id + "F34", { "sketchPlane" : qUnion([Q0])});
            skLineSegment(sketch, "E89.0", {"start": v(304.8, 838.2) * mm, "end": v(304.8, 457.2) * mm});
            skLineSegment(sketch, "E90.0", {"start": v(508, 838.2) * mm, "end": v(508, 457.2) * mm});
            skLineSegment(sketch, "E91.0", {"start": v(406.4, 279.4) * mm, "end": v(406.4, 25.4) * mm});
            skLineSegment(sketch, "E92", {"start": v(304.8, 797.34) * mm, "end": v(254, 797.34) * mm});
            skLineSegment(sketch, "E93", {"start": v(254, 797.34) * mm, "end": v(254, 695.74) * mm});
            skLineSegment(sketch, "E94", {"start": v(254, 695.74) * mm, "end": v(304.8, 695.74) * mm});
            skLineSegment(sketch, "E95", {"start": v(304.8, 695.74) * mm, "end": v(304.8, 797.34) * mm});
            skLineSegment(sketch, "E96", {"start": v(508, 558.8) * mm, "end": v(457.2, 558.8) * mm});
            skLineSegment(sketch, "E97", {"start": v(457.2, 558.8) * mm, "end": v(457.2, 457.2) * mm});
            skLineSegment(sketch, "E98", {"start": v(457.2, 457.2) * mm, "end": v(508, 457.2) * mm});
            skLineSegment(sketch, "E99", {"start": v(508, 558.8) * mm, "end": v(508, 457.2) * mm});
            skLineSegment(sketch, "E100", {"start": v(406.4, 50.44) * mm, "end": v(355.6, 50.44) * mm});
            skLineSegment(sketch, "E101", {"start": v(355.6, 50.44) * mm, "end": v(355.6, 152.04) * mm});
            skLineSegment(sketch, "E102", {"start": v(355.6, 152.04) * mm, "end": v(406.4, 152.04) * mm});
            skLineSegment(sketch, "E103", {"start": v(406.4, 152.04) * mm, "end": v(406.4, 50.44) * mm});
            skSolve(sketch);
        }
        {
            var Q0;
            Q0 = qSketchRegion(id + "F34", true);
            extrude(context, id + "F35", {"entities" : qUnion([Q0]), "operationType" : NewBodyOperationType.ADD, "depth" : 152.4 * mm, "offsetDistance" : 25.4 * mm});
        }
        {
            var Q0;
            {var subQ0=sQuery(id+"F8.wireOp",EDGE,"E20");var subQ1=sQuery(id+"F6.wireOp",EDGE,"E18");var subQ2=sQuery(id+"F6.wireOp",EDGE,"E16");var subQ3=sQuery(id+"F6.wireOp",EDGE,"E13");var subQ10=makeQuery(id+"F3.opExtrude","SWEPT_FACE",FACE,{"disambiguationData":[OSD([sQuery(id+"F2.wireOp",EDGE,"E3")])]});var subQ11=makeQuery(id+"F3.opExtrude","SWEPT_FACE",FACE,{"disambiguationData":[OSD([sQuery(id+"F2.wireOp",EDGE,"E4")])]});var subQ15=makeQuery(id+"F1.opExtrude","CAP_FACE",FACE,{"disambiguationData":[OSD([sQuery(id+"F0.wireOp",EDGE,"E0.bottom"),sQuery(id+"F0.wireOp",EDGE,"E0.top"),sQuery(id+"F0.wireOp",EDGE,"E0.left"),sQuery(id+"F0.wireOp",EDGE,"E0.right")])],"isStart":false});var subQ16=subQ15;var subQ17=makeQuery(id+"F7.boolean.opBoolean","SPLIT",FACE,{"disambiguationData":[TD([subQ11])],"derivedFrom":subQ16});var subQ19=sQuery(id+"F8.wireOp",EDGE,"E21");Q0=makeQuery(id+"F15.boolean.opBoolean","MERGE",FACE,{"derivedFrom":[makeQuery(id+"F9.boolean.opBoolean","SPLIT",FACE,{"disambiguationData":[TD([subQ11])],"derivedFrom":subQ17}),makeQuery(id+"F13.boolean.opBoolean","MERGE",FACE,{"derivedFrom":[makeQuery(id+"F9.boolean.opBoolean","SPLIT",FACE,{"disambiguationData":[TD([makeQuery(id+"F9.opExtrude","SWEPT_FACE",FACE,{"disambiguationData":[OSD([subQ19])]})])],"derivedFrom":subQ17}),makeQuery(id+"F11.boolean.opBoolean","MERGE",FACE,{"derivedFrom":[makeQuery(id+"F7.boolean.opBoolean","SPLIT",FACE,{"disambiguationData":[TD([makeQuery(id+"F7.opExtrude","SWEPT_FACE",FACE,{"disambiguationData":[OSD([sQuery(id+"F6.wireOp",EDGE,"E14")])]})])],"derivedFrom":subQ16}),makeQuery(id+"F7.boolean.opBoolean","SPLIT",FACE,{"disambiguationData":[TD([makeQuery(id+"F7.opExtrude","SWEPT_FACE",FACE,{"disambiguationData":[OSD([sQuery(id+"F6.wireOp",EDGE,"E15")])]})])],"derivedFrom":subQ16}),makeQuery(id+"F9.boolean.opBoolean","SPLIT",FACE,{"disambiguationData":[TD([subQ10])],"derivedFrom":subQ17}),makeQuery(id+"F11.opExtrude","SWEPT_FACE",FACE,{"disambiguationData":[OSD([sQuery(id+"F10.wireOp",EDGE,"E28")])]}),makeQuery(id+"F11.opExtrude","SWEPT_FACE",FACE,{"disambiguationData":[OSD([subQ3,subQ2,subQ1])]})]}),makeQuery(id+"F13.opExtrude","SWEPT_FACE",FACE,{"disambiguationData":[OSD([sQuery(id+"F12.wireOp",EDGE,"E36")])]})]}),makeQuery(id+"F15.opExtrude","SWEPT_FACE",FACE,{"disambiguationData":[OSD([subQ0])]})]});}
            var sketch = newSketch(context, id + "F36", { "sketchPlane" : qUnion([Q0])});
            skLineSegment(sketch, "E104", {"start": v(34.9, 304.8) * mm, "end": v(34.9, 330.2) * mm});
            skLineSegment(sketch, "E105", {"start": v(34.9, 330.2) * mm, "end": v(85.7, 330.2) * mm});
            skLineSegment(sketch, "E106", {"start": v(85.7, 330.2) * mm, "end": v(85.7, 304.8) * mm});
            skLineSegment(sketch, "E107", {"start": v(85.7, 304.8) * mm, "end": v(34.9, 304.8) * mm});
            skEllipse(sketch, "E108", {"center": v(60.37, 356.47) * mm, "majorRadius": 25.4 * mm, "minorRadius": 19.05 * mm, "majorAxis": v(0, 1)});
            skSolve(sketch);
        }
        {
            var Q0;
            Q0 = qSketchRegion(id + "F36", true);
            extrude(context, id + "F37", {"entities" : qUnion([Q0]), "operationType" : NewBodyOperationType.ADD, "depth" : 50.8 * mm, "offsetDistance" : 25.4 * mm});
        }
        {
            var Q0;
            Q0=makeQuery(id+"F37.opExtrude","CAP_FACE",FACE,{"disambiguationData":[OSD([sQuery(id+"F36.wireOp",EDGE,"E104"),sQuery(id+"F36.wireOp",EDGE,"E105"),sQuery(id+"F36.wireOp",EDGE,"E106"),sQuery(id+"F36.wireOp",EDGE,"E107")])],"isStart":false});
            var sketch = newSketch(context, id + "F38", { "sketchPlane" : qUnion([Q0])});
            skLineSegment(sketch, "E109.0", {"start": v(34.9, 330.2) * mm, "end": v(85.7, 330.2) * mm});
            skLineSegment(sketch, "E110.0", {"start": v(85.7, 330.2) * mm, "end": v(85.7, 304.8) * mm});
            skLineSegment(sketch, "E111.0", {"start": v(34.9, 304.8) * mm, "end": v(85.7, 304.8) * mm});
            skLineSegment(sketch, "E112.0", {"start": v(34.9, 304.8) * mm, "end": v(34.9, 330.2) * mm});
            skSolve(sketch);
        }
        {
            var Q0;
            Q0 = qSketchRegion(id + "F38", true);
            extrude(context, id + "F39", {"entities" : qUnion([Q0]), "operationType" : NewBodyOperationType.ADD, "depth" : 25.4 * mm, "offsetDistance" : 25.4 * mm});
        }
    });
